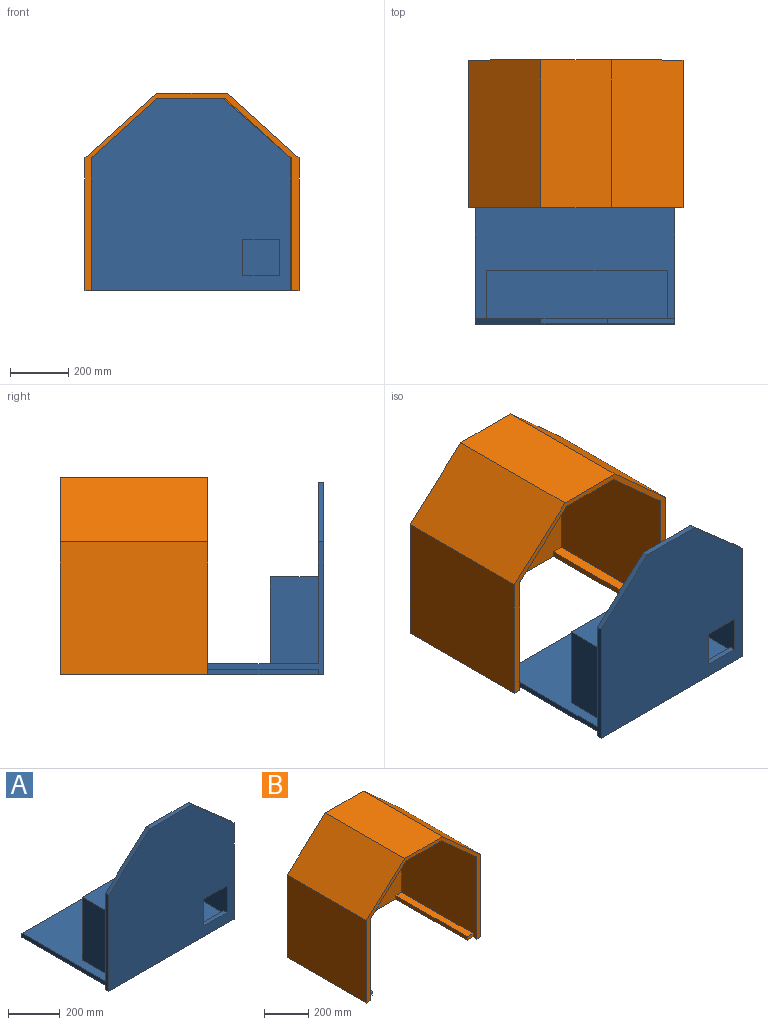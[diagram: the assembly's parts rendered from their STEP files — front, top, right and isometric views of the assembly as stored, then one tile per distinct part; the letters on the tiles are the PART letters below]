
ASSEMBLY  parts=2 mates=1
PART A: 47 faces, bbox 685.8x476.3x660.4 mm
  f0: plane 177.64x152.4mm, normal (0,0,1), area 27073mm2, adj f2,f19,f32,f35
  f1: plane 152.4x152.4mm, normal (0,0,1), area 23225.8mm2, adj f2,f30,f34,f35
  f2: plane 596.9x285.75mm, normal (0,1,0), area 118849.9mm2, adj f0,f1,f18,f19,f20,f24,f30,f31
  f3: plane 685.8x38.1mm, normal (0,1,0), area 14516.1mm2, adj f4,f5,f6,f7,f8,f9,f10,f11
  f4: plane 457.2x19.05mm, normal (-1,0,0), area 8709.7mm2, adj f3,f6,f14,f17
  f5: plane 457.2x19.05mm, normal (1,0,0), area 8709.7mm2, adj f3,f6,f7,f15
  f6: plane 685.8x476.25mm, normal (0,0,-1), area 47903.1mm2, adj f3,f4,f5,f8,f9,f11,f12,f15
  f7: plane 527.05x457.2mm, normal (0,0,-1), area 240967.3mm2, adj f3,f5,f8,f15
  f8: plane 457.2x19.05mm, normal (-1,0,0), area 8709.7mm2, adj f3,f6,f7,f15
  f9: plane 457.2x19.05mm, normal (1,0,0), area 8709.7mm2, adj f3,f6,f10,f16
  f10: plane 457.2x41.28mm, normal (0,0,-1), area 18870.9mm2, adj f3,f9,f12,f16
  f11: plane 476.25x457.2mm, normal (-1,0,0), area 17419.3mm2, adj f3,f6,f13,f14,f17,f23,f25,f26
  f12: plane 476.25x457.2mm, normal (1,0,0), area 17419.3mm2, adj f3,f6,f10,f13,f16,f21,f25,f26
  f13: plane 685.8x457.2mm, normal (0,0,1), area 210806mm2, adj f3,f11,f12,f26,f27,f29,f40
  f14: plane 457.2x41.28mm, normal (0,0,-1), area 18870.9mm2, adj f3,f4,f11,f17
  f15: plane 527.05x19.05mm, normal (0,1,0), area 10040.3mm2, adj f5,f6,f7,f8
  f16: plane 41.28x19.05mm, normal (0,1,0), area 786.3mm2, adj f6,f9,f10,f12
  f17: plane 41.28x19.05mm, normal (0,1,0), area 786.3mm2, adj f4,f6,f11,f14
  f18: plane 127x19.05mm, normal (0,0,-1), area 2419.4mm2, adj f2,f19,f24,f25
  f19: plane 285.75x171.45mm, normal (-1,0,0), area 45967.7mm2, adj f0,f2,f18,f20,f25,f31,f35
  f20: plane 127x19.05mm, normal (0,0,1), area 2419.4mm2, adj f2,f19,f24,f25
  f21: plane 231.66x203.2mm, normal (0.66,0,0.75), area 5870.3mm2, adj f12,f22,f25,f26
  f22: plane 228.6x19.05mm, normal (0,0,1), area 4354.8mm2, adj f21,f23,f25,f26
  f23: plane 225.54x203.2mm, normal (-0.67,0,0.74), area 5783.1mm2, adj f11,f22,f25,f26
  f24: plane 127x19.05mm, normal (1,0,0), area 2419.4mm2, adj f2,f18,f20,f25
  f25: plane 685.8x660.4mm, normal (0,-1,0), area 390321.8mm2, adj f6,f11,f12,f18,f19,f20,f21,f22
  f26: plane 685.8x622.3mm, normal (0,1,0), area 194596.4mm2, adj f11,f12,f13,f21,f22,f23,f27,f28
  f27: plane 298.45x165.1mm, normal (1,0,0), area 49274.1mm2, adj f13,f26,f28,f40
  f28: plane 622.3x165.1mm, normal (0,0,1), area 102741.7mm2, adj f26,f27,f29,f40
  f29: plane 298.45x165.1mm, normal (-1,0,0), area 49274.1mm2, adj f13,f26,f28,f40
  f30: plane 285.75x152.4mm, normal (1,0,0), area 43548.3mm2, adj f1,f2,f31,f35
  f31: plane 596.9x152.4mm, normal (0,0,-1), area 90967.6mm2, adj f2,f19,f30,f35
  f32: plane 152.4x133.35mm, normal (1,0,0), area 20322.5mm2, adj f0,f2,f33,f35
  f33: plane 266.86x152.4mm, normal (0,0,1), area 40668.8mm2, adj f2,f32,f34,f35
  f34: plane 152.4x133.35mm, normal (-1,0,0), area 20322.5mm2, adj f1,f2,f33,f35
  f35: plane 596.9x285.75mm, normal (0,-1,0), area 118849.9mm2, adj f0,f1,f19,f30,f31,f32,f33,f34
  f36: plane 127x12.7mm, normal (-1,0,0), area 1612.9mm2, adj f35,f37,f39,f40
  f37: plane 127x12.7mm, normal (0,0,-1), area 1612.9mm2, adj f35,f36,f38,f40
  f38: plane 127x12.7mm, normal (1,0,0), area 1612.9mm2, adj f35,f37,f39,f40
  f39: plane 127x12.7mm, normal (0,0,1), area 1612.9mm2, adj f35,f36,f38,f40
  f40: plane 622.3x298.45mm, normal (0,1,0), area 169596.4mm2, adj f13,f27,f28,f29,f36,f37,f38,f39
  f41: plane 241.46x120.65mm, normal (0,-1,0), area 29131.7mm2, adj f43,f44,f45,f46
  f42: plane 241.46x120.65mm, normal (0,1,0), area 29131.7mm2, adj f43,f44,f45,f46
  f43: plane 241.46x152.4mm, normal (0,0,-1), area 36797.9mm2, adj f41,f42,f44,f45
  f44: plane 152.4x120.65mm, normal (1,0,0), area 18387.1mm2, adj f41,f42,f43,f46
  f45: plane 152.4x120.65mm, normal (-1,0,0), area 18387.1mm2, adj f41,f42,f43,f46
  f46: plane 241.46x152.4mm, normal (0,0,1), area 36797.9mm2, adj f41,f42,f44,f45
PART B: 22 faces, bbox 736.6x508x679.5 mm
  f0: plane 685.8x660.4mm, normal (0,-1,0), area 404377.3mm2, adj f1,f2,f7,f8,f9,f10,f11,f12
  f1: plane 482.6x457.2mm, normal (1,0,0), area 211935.1mm2, adj f0,f6,f7,f10,f16,f18
  f2: plane 482.6x457.2mm, normal (-1,0,0), area 211935.1mm2, adj f0,f6,f7,f11,f20,f21
  f3: plane 508x457.2mm, normal (1,0,0), area 232257.6mm2, adj f4,f6,f7,f15
  f4: plane 736.6x679.45mm, normal (0,1,0), area 445657.3mm2, adj f3,f5,f7,f13,f14,f15
  f5: plane 508x457.2mm, normal (-1,0,0), area 232257.6mm2, adj f4,f6,f7,f13
  f6: plane 736.6x679.45mm, normal (0,-1,0), area 39828.4mm2, adj f1,f2,f3,f5,f7,f8,f9,f10
  f7: plane 736.6x508mm, normal (0,0,-1), area 78064.4mm2, adj f0,f1,f2,f3,f4,f5,f6,f16
  f8: plane 482.6x225.54mm, normal (-0.67,0,-0.74), area 146505.8mm2, adj f0,f6,f11,f12
  f9: plane 482.6x225.54mm, normal (0.67,0,-0.74), area 146505.8mm2, adj f0,f6,f10,f12
  f10: plane 482.6x3.06mm, normal (0,0,-1), area 1476.9mm2, adj f0,f1,f6,f9
  f11: plane 482.6x3.06mm, normal (0,0,-1), area 1476.9mm2, adj f0,f2,f6,f8
  f12: plane 482.6x228.6mm, normal (0,0,-1), area 110322.4mm2, adj f0,f6,f8,f9
  f13: plane 508x246.68mm, normal (-0.67,0,0.74), area 168674.4mm2, adj f4,f5,f6,f14
  f14: plane 508x243.23mm, normal (0,0,1), area 123561.8mm2, adj f4,f6,f13,f15
  f15: plane 508x246.68mm, normal (0.67,0,0.74), area 168674.4mm2, adj f3,f4,f6,f14
  f16: plane 38.1x19.05mm, normal (0,-1,0), area 725.8mm2, adj f1,f7,f17,f18
  f17: plane 457.2x19.05mm, normal (1,0,0), area 8709.7mm2, adj f0,f7,f16,f18
  f18: plane 457.2x38.1mm, normal (0,0,1), area 17419.3mm2, adj f0,f1,f16,f17
  f19: plane 457.2x19.05mm, normal (-1,0,0), area 8709.7mm2, adj f0,f7,f20,f21
  f20: plane 38.1x19.05mm, normal (0,-1,0), area 725.8mm2, adj f2,f7,f19,f21
  f21: plane 457.2x38.1mm, normal (0,0,1), area 17419.3mm2, adj f0,f2,f19,f20
PLACE A t=(-3.17,-635,0)mm
PLACE B t=(0,-228.6,0)mm
MATE slider B.f16 <-> A.f17  axis (0,-1,0) through (-304.8,-457.2,0)mm
